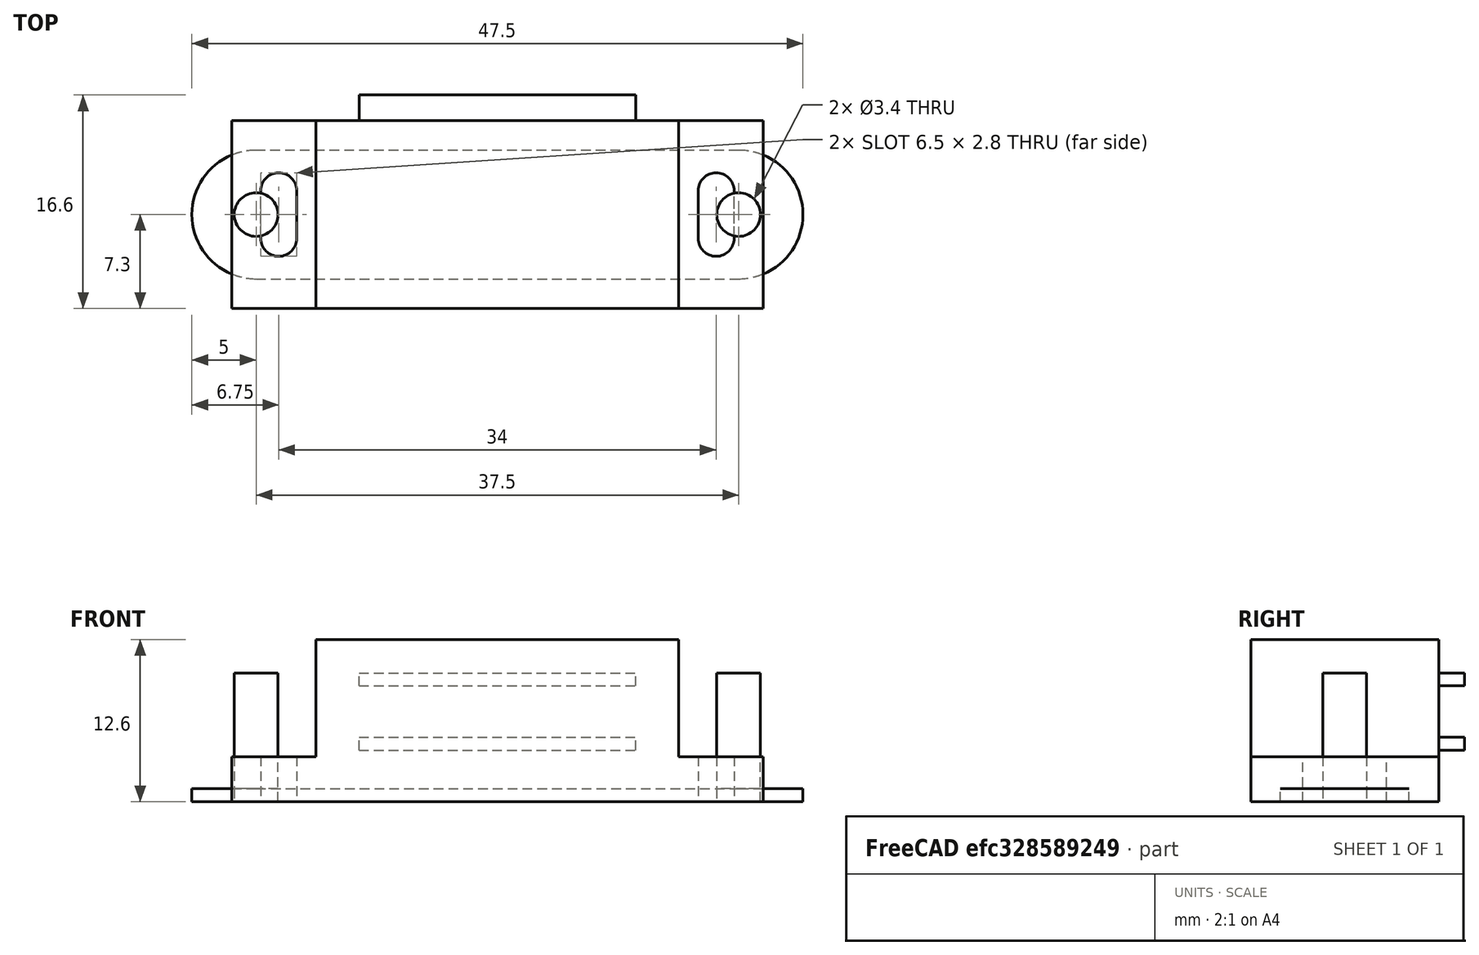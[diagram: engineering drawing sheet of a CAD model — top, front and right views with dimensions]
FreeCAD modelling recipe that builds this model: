
FCSTD DOCUMENT  (FreeCAD 0.22R37100 (Git))
Label: magnet_fix
License: All rights reserved
LicenseURL: http://en.wikipedia.org/wiki/All_rights_reserved
objects: Sketcher::SketchObject×10, PartDesign::SubShapeBinder×4, PartDesign::Pad×4, TechDraw::DrawViewDimension×3, PartDesign::Body×2, TechDraw::DrawViewPart×2, PartDesign::Pocket×1, Spreadsheet::Sheet×1, PartDesign::CoordinateSystem×1, PartDesign::LinearPattern×1, Part::Mirroring×1, Part::FeaturePython×1, Part::Extrusion×1, Part::Compound×1, PartDesign::Boolean×1, Part::Feature×1, TechDraw::DrawSVGTemplate×1, TechDraw::DrawPage×1
note: 39 computed .brp shape members not serialized (recipe doc carries the construction recipe); baked Part::Feature solids carry a one-line shape summary decoded from their .brp

FEATURE [Sketcher::SketchObject] Sketch
  FullyConstrained = true
  sketch-geometry (5):
    g0: LineSegment StartX=-20.65 StartY=-7.3 StartZ=0 EndX=20.65 EndY=-7.3 EndZ=0
    g1: LineSegment StartX=20.65 StartY=-7.3 StartZ=0 EndX=20.65 EndY=7.3 EndZ=0
    g2: LineSegment StartX=20.65 StartY=7.3 StartZ=0 EndX=-20.65 EndY=7.3 EndZ=0
    g3: LineSegment StartX=-20.65 StartY=7.3 StartZ=0 EndX=-20.65 EndY=-7.3 EndZ=0
    g4: GeomPoint X=0 Y=0 Z=0
  constraints (12):
    c: Coincident(g0,g1)
    c: Coincident(g1,g2)
    c: Coincident(g2,g3)
    c: Coincident(g3,g0)
    c: Horizontal(g0)
    c: Horizontal(g2)
    c: Vertical(g1)
    c: Vertical(g3)
    c: Symmetric(g2,g0,g4)
    c: Coincident(g4,g-1)
    c: DistanceX(g0,g1) = 41.3
    c: DistanceY(g0,g1) = 14.6
FEATURE [Sketcher::SketchObject] Sketch001
  ExternalGeometry = -> [Sketch]
  FullyConstrained = true
  sketch-geometry (5):
    g0: LineSegment StartX=-14.1 StartY=-7.3 StartZ=0 EndX=14.1 EndY=-7.3 EndZ=0
    g1: LineSegment StartX=14.1 StartY=-7.3 StartZ=0 EndX=14.1 EndY=7.3 EndZ=0
    g2: LineSegment StartX=14.1 StartY=7.3 StartZ=0 EndX=-14.1 EndY=7.3 EndZ=0
    g3: LineSegment StartX=-14.1 StartY=7.3 StartZ=0 EndX=-14.1 EndY=-7.3 EndZ=0
    g4: GeomPoint X=0 Y=0 Z=0
  constraints (12):
    c: Coincident(g0,g1)
    c: Coincident(g1,g2)
    c: Coincident(g2,g3)
    c: Coincident(g3,g0)
    c: Horizontal(g0)
    c: Horizontal(g2)
    c: Vertical(g1)
    c: Vertical(g3)
    c: Symmetric(g2,g0,g4)
    c: Coincident(g4,g-1)
    c: Horizontal(g1,g-3)
    c: DistanceX(g2,g2) = 28.2
FEATURE [Sketcher::SketchObject] Sketch002  label="holes"
  FullyConstrained = true
  sketch-geometry (10):
    g0: ArcOfCircle CenterX=17 CenterY=-1.85 CenterZ=0 NormalX=0 NormalY=0 NormalZ=1 AngleXU=0 Radius=1.4 StartAngle=3.14159 EndAngle=6.28319
    g1: ArcOfCircle CenterX=17 CenterY=1.85 CenterZ=0 NormalX=0 NormalY=0 NormalZ=1 AngleXU=0 Radius=1.4 StartAngle=0 EndAngle=3.14159
    g2: LineSegment StartX=15.6 StartY=-1.85 StartZ=0 EndX=15.6 EndY=1.85 EndZ=0
    g3: LineSegment StartX=18.4 StartY=-1.85 StartZ=0 EndX=18.4 EndY=1.85 EndZ=0
    g4: ArcOfCircle CenterX=-17 CenterY=-1.85 CenterZ=0 NormalX=0 NormalY=0 NormalZ=1 AngleXU=0 Radius=1.4 StartAngle=3.14159 EndAngle=6.28319
    g5: ArcOfCircle CenterX=-17 CenterY=1.85 CenterZ=0 NormalX=0 NormalY=0 NormalZ=1 AngleXU=0 Radius=1.4 StartAngle=0 EndAngle=3.14159
    g6: LineSegment StartX=-18.4 StartY=-1.85 StartZ=0 EndX=-18.4 EndY=1.85 EndZ=0
    g7: LineSegment StartX=-15.6 StartY=-1.85 StartZ=0 EndX=-15.6 EndY=1.85 EndZ=0
    g8: GeomPoint X=17 Y=-3.25 Z=0
    g9: GeomPoint X=17 Y=3.25 Z=0
  constraints (22):
    c: Tangent(g0,g2) = 1.5708
    c: Tangent(g0,g3) = -1.5708
    c: Tangent(g1,g2) = 1.5708
    c: Tangent(g1,g3) = -1.5708
    c: Equal(g0,g1)
    c: Vertical(g3)
    c: Tangent(g4,g6) = 1.5708
    c: Tangent(g4,g7) = -1.5708
    c: Tangent(g5,g6) = 1.5708
    c: Tangent(g5,g7) = -1.5708
    c: Equal(g4,g5)
    c: Vertical(g6)
    c: PointOnObject(g8,g0)
    c: PointOnObject(g9,g1)
    c: Vertical(g9,g0)
    c: Symmetric(g8,g9,g-1)
    c: DistanceY(g8,g9) = 6.5
    c: DistanceX(g0,g0) = 2.8
    c: Symmetric(g4,g1,g-1)
    c: Equal(g7,g2)
    c: Equal(g5,g1)
    c: DistanceX(g4,g0) = 34
FEATURE [PartDesign::SubShapeBinder] Binder
  BindCopyOnChange = 0
  BindMode = 0
  ClaimChildren = false
  Context = -> Body [Binder.]
  Fuse = false
  MakeFace = true
  OffsetFill = false
  OffsetIntersection = false
  OffsetJoinType = 0
  OffsetOpenResult = false
  PartialLoad = false
  Relative = true
  Support = -> [Sketch]
  _Version = 2
FEATURE [PartDesign::Pad] Pad
  Direction = (0,0,1)
  Length = 3.5
  Length2 = 10
  Profile = -> Binder
  Suppressed = false
  Type = 0
FEATURE [PartDesign::SubShapeBinder] Binder001
  BindCopyOnChange = 0
  BindMode = 0
  ClaimChildren = false
  Context = -> Body [Binder001.]
  Fuse = false
  MakeFace = true
  OffsetFill = false
  OffsetIntersection = false
  OffsetJoinType = 0
  OffsetOpenResult = false
  PartialLoad = false
  Relative = true
  Support = -> [Sketch001]
  _Version = 2
FEATURE [PartDesign::Pad] Pad001
  BaseFeature = -> Pad
  Direction = (0,0,1)
  Length = 12.6
  Length2 = 10
  Profile = -> Binder001
  Suppressed = false
  Type = 0
FEATURE [PartDesign::SubShapeBinder] Binder002
  BindCopyOnChange = 0
  BindMode = 0
  ClaimChildren = false
  Context = -> Body [Binder002.]
  Fuse = false
  MakeFace = true
  OffsetFill = false
  OffsetIntersection = false
  OffsetJoinType = 0
  OffsetOpenResult = false
  PartialLoad = false
  Relative = true
  Support = -> [Sketch002]
  _Version = 2
FEATURE [PartDesign::Pocket] Pocket
  BaseFeature = -> Pad001
  Direction = (0,0,-1)
  Length = 5
  Length2 = 5
  Midplane = true
  Profile = -> Binder002
  Suppressed = false
  Type = 1
FEATURE [Sketcher::SketchObject] Sketch003
  ExternalGeometry = -> [Sketch001]
  FullyConstrained = true
  sketch-geometry (5):
    g0: LineSegment StartX=-10.75 StartY=7.3 StartZ=0 EndX=10.75 EndY=7.3 EndZ=0
    g1: LineSegment StartX=10.75 StartY=7.3 StartZ=0 EndX=10.75 EndY=9.3 EndZ=0
    g2: LineSegment StartX=10.75 StartY=9.3 StartZ=0 EndX=-10.75 EndY=9.3 EndZ=0
    g3: LineSegment StartX=-10.75 StartY=9.3 StartZ=0 EndX=-10.75 EndY=7.3 EndZ=0
    g4: GeomPoint X=0 Y=8.3 Z=0
  constraints (13):
    c: Coincident(g0,g1)
    c: Coincident(g1,g2)
    c: Coincident(g2,g3)
    c: Coincident(g3,g0)
    c: Horizontal(g0)
    c: Horizontal(g2)
    c: Vertical(g1)
    c: Vertical(g3)
    c: PointOnObject(g4,g-2)
    c: Symmetric(g0,g1,g4)
    c: DistanceX(g0,g0) = 21.5
    c: PointOnObject(g0,g-3)
    c: DistanceY(g1,g1) = 2
FEATURE [Spreadsheet::Sheet] Spreadsheet  label="Properties"
  cells = B2(length)==41.3 mm; C2(width)==16.6 mm
FEATURE [PartDesign::CoordinateSystem] Local_CS
  AttacherType = Attacher::AttachEngine3D
  AttachmentSupport = -> [XY_Plane]
  MapMode = 5
FEATURE [Sketcher::SketchObject] Sketch004
  AttachmentOffset = pos=(0,0,4) rot=(0,0,1;0rad)
  AttachmentSupport = -> [XY_Plane]
  FullyConstrained = true
  MapMode = 5
  Placement = pos=(0,0,4) rot=(0,0,1;0rad)
  sketch-geometry (4):
    g0: LineSegment StartX=-10.75 StartY=7.3 StartZ=0 EndX=10.75 EndY=7.3 EndZ=0
    g1: LineSegment StartX=10.75 StartY=7.3 StartZ=0 EndX=10.75 EndY=9.3 EndZ=0
    g2: LineSegment StartX=10.75 StartY=9.3 StartZ=0 EndX=-10.75 EndY=9.3 EndZ=0
    g3: LineSegment StartX=-10.75 StartY=9.3 StartZ=0 EndX=-10.75 EndY=7.3 EndZ=0
  constraints (11):
    c: Coincident(g0,g1)
    c: Coincident(g1,g2)
    c: Coincident(g2,g3)
    c: Coincident(g3,g0)
    c: Horizontal(g0)
    c: Vertical(g1)
    c: Vertical(g3)
    c: DistanceY(g1,g1) = 2
    c: DistanceY(g0) = 7.3
    c: Symmetric(g2,g1,g-2)
    c: DistanceX(g0,g0) = 21.5
FEATURE [PartDesign::Pad] Pad002
  BaseFeature = -> Pocket
  Direction = (0,0,1)
  Length = 1
  Length2 = 10
  Profile = -> Sketch004
  ReferenceAxis = -> Sketch004 [N_Axis]
  Suppressed = false
  Type = 0
FEATURE [PartDesign::LinearPattern] LinearPattern
  BaseFeature = -> Pad002
  Direction = -> Z_Axis
  Length = 5
  Mode = 0
  Occurrences = 2
  Offset = 5
  Originals = -> [Pad002]
  Refine = true
  Suppressed = false
FEATURE [PartDesign::Body] Body
  Group = -> [Binder,Pad,Binder001,Pad001,Binder002,Pocket,Local_CS,Sketch004,Pad002,LinearPattern]
  Origin = -> Origin
  Tip = -> LinearPattern
FEATURE [Sketcher::SketchObject] Sketch006  label="magnet_fix_reply_holes"
  ExternalGeometry = -> [Sketch003]
  FullyConstrained = true
  sketch-geometry (2):
    g0: Circle CenterX=18.75 CenterY=0 CenterZ=0 NormalX=0 NormalY=0 NormalZ=1 AngleXU=0 Radius=1.7
    g1: Circle CenterX=-18.75 CenterY=0 CenterZ=0 NormalX=0 NormalY=0 NormalZ=1 AngleXU=0 Radius=1.7
  constraints (5):
    c: PointOnObject(g0,g-1)
    c: Symmetric(g0,g1,g-2)
    c: Equal(g1,g0)
    c: Diameter(g1) = 3.4
    c: DistanceX(g-3,g0) = 8
FEATURE [Sketcher::SketchObject] Sketch005
  ExternalGeometry = -> [Sketch006]
  FullyConstrained = true
  sketch-geometry (3):
    g0: ArcOfCircle CenterX=18.75 CenterY=0 CenterZ=0 NormalX=0 NormalY=0 NormalZ=1 AngleXU=0 Radius=5 StartAngle=4.71239 EndAngle=7.85398
    g1: LineSegment StartX=0 StartY=5 StartZ=0 EndX=18.75 EndY=5 EndZ=0
    g2: LineSegment StartX=0 StartY=-5 StartZ=0 EndX=18.75 EndY=-5 EndZ=0
  constraints (8):
    c: PointOnObject(g1,g-2)
    c: Horizontal(g1)
    c: PointOnObject(g2,g-2)
    c: Horizontal(g2)
    c: Tangent(g2,g0) = -1.5708
    c: Tangent(g1,g0) = 1.5708
    c: Coincident(g0,g-3)
    c: DistanceY(g2,g1) = 10
FEATURE [Part::Mirroring] Part__Mirroring  label="Sketch005 (Mirror #1)"
  Base = (0,0,0)
  Normal = (1,0,0)
  Source = -> Sketch005
FEATURE [Part::FeaturePython] Connect  # WARN: FeaturePython — macro-defined, semantics opaque (R4)
  Objects = -> [Sketch005,Part__Mirroring]
  Tolerance = 0
FEATURE [PartDesign::SubShapeBinder] Binder003
  BindCopyOnChange = 0
  BindMode = 0
  ClaimChildren = true
  Context = -> Body001 [Binder003.]
  Fuse = false
  MakeFace = true
  OffsetFill = false
  OffsetIntersection = false
  OffsetJoinType = 0
  OffsetOpenResult = false
  PartialLoad = false
  Relative = false
  Support = -> [Connect]
  _Version = 2
FEATURE [PartDesign::Pad] Pad003
  Direction = (0,0,1)
  Length = 1
  Length2 = 10
  Profile = -> Binder003
  Refine = true
  Suppressed = false
  Type = 0
FEATURE [Part::Extrusion] Extrude
  Base = -> Sketch006
  Dir = (0,0,1)
  DirMode = 2
  FaceMakerClass = Part::FaceMakerBullseye
  LengthFwd = 10
  LengthRev = 0
  Solid = true
  Symmetric = false
FEATURE [Part::Compound] Compound
  Links = -> [Extrude]
FEATURE [PartDesign::Boolean] Boolean
  BaseFeature = -> Pad003
  Group = -> [Compound]
  Suppressed = false
  Type = 1
  UsePlacement = true
FEATURE [PartDesign::Body] Body001  label="magnet_fix_reply"
  Group = -> [Binder003,Pad003,Boolean]
  Origin = -> Origin001
  Tip = -> Boolean
FEATURE [Part::Feature] Unfold
  shape: bbox 47.5 x 10 x 1 mm, 8 faces (baked)
FEATURE [Sketcher::SketchObject] Unfold_Sketch
  FullyConstrained = false
  sketch-geometry (6):
    g0: ArcOfCircle CenterX=-18.75 CenterY=0 CenterZ=0 NormalX=0 NormalY=0 NormalZ=1 AngleXU=-3.14159 Radius=5 StartAngle=4.71239 EndAngle=7.85398
    g1: LineSegment StartX=18.75 StartY=5 StartZ=0 EndX=-18.75 EndY=5 EndZ=0
    g2: LineSegment StartX=-18.75 StartY=-5 StartZ=0 EndX=18.75 EndY=-5 EndZ=0
    g3: ArcOfCircle CenterX=18.75 CenterY=0 CenterZ=0 NormalX=0 NormalY=0 NormalZ=1 AngleXU=0 Radius=5 StartAngle=4.71239 EndAngle=7.85398
    g4: Circle CenterX=-18.75 CenterY=0 CenterZ=0 NormalX=0 NormalY=0 NormalZ=-1 AngleXU=-3.14159 Radius=1.7
    g5: Circle CenterX=18.75 CenterY=0 CenterZ=0 NormalX=0 NormalY=0 NormalZ=-1 AngleXU=-3.14159 Radius=1.7
FEATURE [Sketcher::SketchObject] Unfold_Sketch_Outline
  FullyConstrained = false
  sketch-geometry (4):
    g0: ArcOfCircle CenterX=-18.75 CenterY=0 CenterZ=0 NormalX=0 NormalY=0 NormalZ=1 AngleXU=-3.14159 Radius=5 StartAngle=4.71239 EndAngle=7.85398
    g1: LineSegment StartX=-18.75 StartY=-5 StartZ=0 EndX=18.75 EndY=-5 EndZ=0
    g2: ArcOfCircle CenterX=18.75 CenterY=0 CenterZ=0 NormalX=0 NormalY=0 NormalZ=1 AngleXU=0 Radius=5 StartAngle=4.71239 EndAngle=7.85398
    g3: LineSegment StartX=18.75 StartY=5 StartZ=0 EndX=-18.75 EndY=5 EndZ=0
FEATURE [Sketcher::SketchObject] Unfold_Sketch_Internal
  FullyConstrained = false
  sketch-geometry (2):
    g0: Circle CenterX=18.75 CenterY=0 CenterZ=0 NormalX=0 NormalY=0 NormalZ=-1 AngleXU=-3.14159 Radius=1.7
    g1: Circle CenterX=-18.75 CenterY=0 CenterZ=0 NormalX=0 NormalY=0 NormalZ=-1 AngleXU=-3.14159 Radius=1.7
FEATURE [TechDraw::DrawSVGTemplate] Template
  Height = 210
  Orientation = 1
  Template = <path>
  Width = 297
FEATURE [TechDraw::DrawViewPart] View
  CoarseView = false
  Direction = (0,0,1)
  Focus = 100
  HardHidden = false
  IsoCount = 0
  IsoHidden = false
  IsoVisible = false
  LockPosition = false
  Perspective = false
  Rotation = 0
  Scale = 4
  ScaleType = 2
  ScrubCount = 0
  SeamHidden = false
  SeamVisible = true
  SmoothHidden = false
  SmoothVisible = true
  Source = -> [Body001]
  X = 112.5
  XDirection = (1,0,0)
  Y = 45
FEATURE [TechDraw::DrawViewPart] View001
  CoarseView = false
  Direction = (0.57735,-0.57735,0.57735)
  Focus = 100
  HardHidden = false
  IsoCount = 0
  IsoHidden = false
  IsoVisible = false
  LockPosition = false
  Perspective = false
  Rotation = 0
  Scale = 4
  ScaleType = 2
  ScrubCount = 0
  SeamHidden = false
  SeamVisible = true
  SmoothHidden = false
  SmoothVisible = true
  Source = -> [Body001]
  X = 208.5
  XDirection = (0.707107,0.707107,0)
  Y = 135
FEATURE [TechDraw::DrawViewDimension] Dimension
  AngleOverride = false
  Arbitrary = false
  ArbitraryTolerances = false
  BoxCorners = (2) [(-95,-20,0),(95,20,0)]
  EqualTolerance = true
  ExtensionAngle = 0
  FormatSpec = %.2w
  FormatSpecOverTolerance = %+.2w
  FormatSpecUnderTolerance = %+.2w
  Inverted = false
  LineAngle = 0
  LockPosition = false
  MeasureType = 1
  OverTolerance = 0
  References2D = -> [View]
  Rotation = 0
  ScaleType = 0
  TheoreticalExact = false
  Type = 1
  UnderTolerance = 0
  X = 0.61437
  Y = 32.297
FEATURE [TechDraw::DrawViewDimension] Dimension001
  AngleOverride = false
  Arbitrary = false
  ArbitraryTolerances = false
  BoxCorners = (2) [(-95,-20,0),(95,20,0)]
  EqualTolerance = true
  ExtensionAngle = 0
  FormatSpec = %.2w
  FormatSpecOverTolerance = %+.2w
  FormatSpecUnderTolerance = %+.2w
  Inverted = false
  LineAngle = 0
  LockPosition = false
  MeasureType = 1
  OverTolerance = 0
  References2D = -> [View]
  Rotation = 0
  ScaleType = 0
  TheoreticalExact = false
  Type = 2
  UnderTolerance = 0
  X = 110.554
  Y = -0.759103
FEATURE [TechDraw::DrawViewDimension] Dimension002
  AngleOverride = false
  Arbitrary = false
  ArbitraryTolerances = false
  BoxCorners = (2) [(-95,-20,0),(95,20,0)]
  EqualTolerance = true
  ExtensionAngle = 0
  FormatSpec = R%.2w
  FormatSpecOverTolerance = %+.2w
  FormatSpecUnderTolerance = %+.2w
  Inverted = false
  LineAngle = 0
  LockPosition = false
  MeasureType = 1
  OverTolerance = 0
  References2D = -> [View]
  Rotation = 0
  ScaleType = 0
  TheoreticalExact = false
  Type = 4
  UnderTolerance = 0
  X = -53.9727
  Y = 5.80719
FEATURE [TechDraw::DrawPage] Page
  KeepUpdated = true
  NextBalloonIndex = 1
  ProjectionType = 0
  Template = -> Template
  Views = -> [View,View001,Dimension,Dimension001,Dimension002]
note: 1 file-system path scrubbed to <path> (originals preserved in the JSON sidecar)
